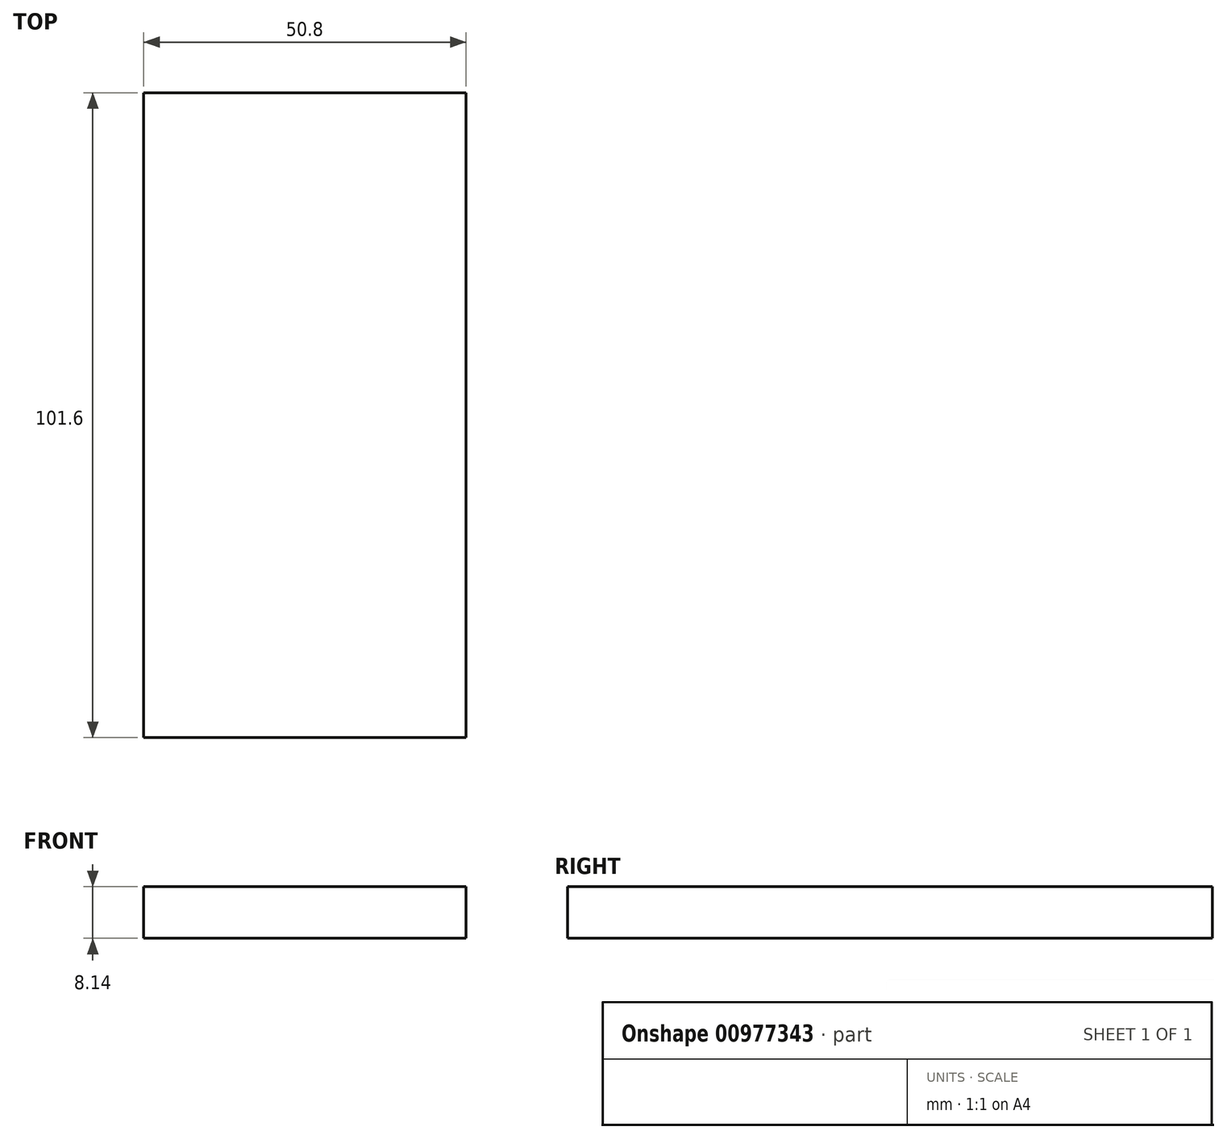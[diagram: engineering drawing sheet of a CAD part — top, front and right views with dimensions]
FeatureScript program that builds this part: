
annotation { "Feature Type Name" : "Feature", "Feature Type Description" : "" }
export const myFeature = defineFeature(function(context is Context, id is Id, definition is map)
    precondition{}
    {
        {
            var Q0;
            Q0=qCreatedBy(makeId("Front.planeOp"),FACE);
            var sketch = newSketch(context, id + "F0", { "sketchPlane" : qUnion([Q0])});
            skLineSegment(sketch, "E0.bottom", {"start": v(25.7, 55.49) * mm, "end": v(-25.1, 55.49) * mm});
            skLineSegment(sketch, "E0.top", {"start": v(25.7, -71.51) * mm, "end": v(-25.1, -71.51) * mm});
            skLineSegment(sketch, "E0.left", {"start": v(25.7, 55.49) * mm, "end": v(25.7, -71.51) * mm});
            skLineSegment(sketch, "E0.right", {"start": v(-25.1, 55.49) * mm, "end": v(-25.1, -71.51) * mm});
            skLineSegment(sketch, "E1", {"start": v(-25.1, 25.7) * mm, "end": v(25.7, 25.7) * mm});
            skLineSegment(sketch, "E2", {"start": v(-25.1, 0) * mm, "end": v(25.7, 0) * mm});
            skLineSegment(sketch, "E3", {"start": v(-25.1, 17.55) * mm, "end": v(25.7, 17.55) * mm});
            skSolve(sketch);
        }
        {
            var Q0;
            {var subQ0=sQuery(id+"F0.wireOp",EDGE,"E1");Q0=makeQuery(id+"F0.imprint","IMPRINT",FACE,{"disambiguationData":[TD([[makeQuery(id+"F0.imprint","IMPRINT",EDGE,{"derivedFrom":subQ0}),-1.0]])]});}
            extrude(context, id + "F1", {"entities" : qUnion([Q0]), "depth" : 101.6 * mm, "offsetDistance" : 25.4 * mm});
        }
    });
